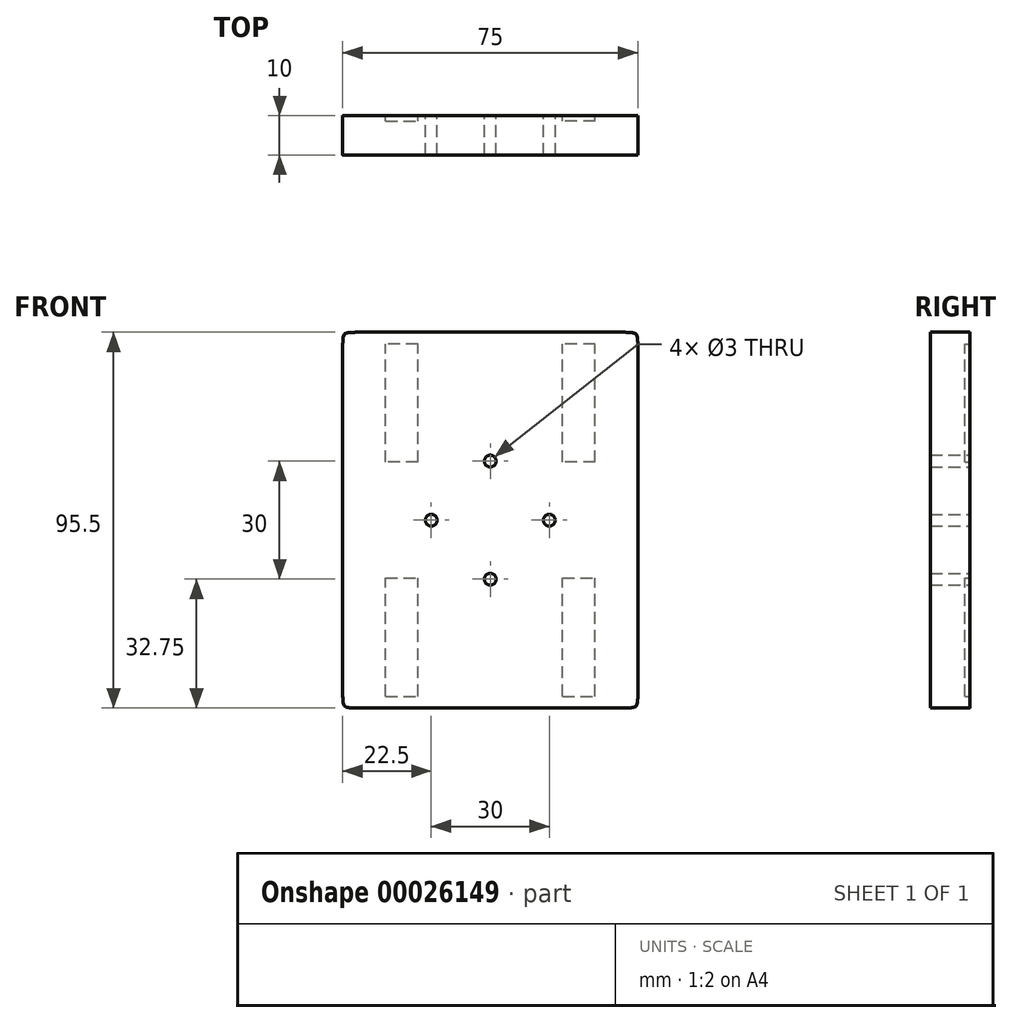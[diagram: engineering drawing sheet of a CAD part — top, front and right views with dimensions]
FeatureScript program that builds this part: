
annotation { "Feature Type Name" : "Feature", "Feature Type Description" : "" }
export const myFeature = defineFeature(function(context is Context, id is Id, definition is map)
    precondition{}
    {
        {
            var Q0;
            Q0=qCreatedBy(makeId("Front.planeOp"),FACE);
            var sketch = newSketch(context, id + "F0", { "sketchPlane" : qUnion([Q0])});
            skLineSegment(sketch, "E0.rect.bottom", {"start": v(37.5, -47.75) * mm, "end": v(-37.5, -47.75) * mm});
            skLineSegment(sketch, "E0.rect.top", {"start": v(37.5, 47.75) * mm, "end": v(-37.5, 47.75) * mm});
            skLineSegment(sketch, "E0.rect.left", {"start": v(37.5, -47.75) * mm, "end": v(37.5, 47.75) * mm});
            skLineSegment(sketch, "E0.rect.right", {"start": v(-37.5, -47.75) * mm, "end": v(-37.5, 47.75) * mm});
            skPoint(sketch, "E0.rect.middle", {"position": v(0, 0) * mm});
            skLineSegment(sketch, "E1", {"start": v(0, 15) * mm, "end": v(0, -15) * mm, "construction": true});
            skLineSegment(sketch, "E2", {"start": v(15, 0) * mm, "end": v(-15, 0) * mm, "construction": true});
            skCircle(sketch, "E3", {"center": v(0, 15) * mm, "radius": 1.5 * mm});
            skCircle(sketch, "E4", {"center": v(-15, 0) * mm, "radius": 1.5 * mm});
            skCircle(sketch, "E5", {"center": v(15, 0) * mm, "radius": 1.5 * mm});
            skCircle(sketch, "E6", {"center": v(0, -15) * mm, "radius": 1.5 * mm});
            skPoint(sketch, "E7.orphan", {"position": v(0, 47.75) * mm});
            skPoint(sketch, "E8.orphan", {"position": v(-37.5, 0) * mm});
            skPoint(sketch, "E9.orphan", {"position": v(0, -47.75) * mm});
            skPoint(sketch, "E10.orphan", {"position": v(37.5, 0) * mm});
            skLineSegment(sketch, "E11", {"start": v(22.5, 47.75) * mm, "end": v(22.5, -47.75) * mm, "construction": true});
            skLineSegment(sketch, "E12", {"start": v(-22.5, 47.75) * mm, "end": v(-22.5, -47.75) * mm, "construction": true});
            skLineSegment(sketch, "E13", {"start": v(-22.5, -47.75) * mm, "end": v(22.5, 47.75) * mm, "construction": true});
            skLineSegment(sketch, "E14.rect.bottom", {"start": v(-18.37, 14.75) * mm, "end": v(-26.62, 14.75) * mm});
            skLineSegment(sketch, "E14.rect.top", {"start": v(-18.38, 44.75) * mm, "end": v(-26.63, 44.75) * mm});
            skLineSegment(sketch, "E14.rect.left", {"start": v(-18.37, 14.75) * mm, "end": v(-18.38, 44.75) * mm});
            skLineSegment(sketch, "E14.rect.right", {"start": v(-26.62, 14.75) * mm, "end": v(-26.63, 44.75) * mm});
            skPoint(sketch, "E14.rect.middle", {"position": v(-22.5, 29.75) * mm});
            skLineSegment(sketch, "E15.rect.bottom", {"start": v(-26.62, -44.75) * mm, "end": v(-18.37, -44.75) * mm});
            skLineSegment(sketch, "E15.rect.top", {"start": v(-26.62, -14.75) * mm, "end": v(-18.38, -14.75) * mm});
            skLineSegment(sketch, "E15.rect.left", {"start": v(-26.62, -44.75) * mm, "end": v(-26.62, -14.75) * mm});
            skLineSegment(sketch, "E15.rect.right", {"start": v(-18.37, -44.75) * mm, "end": v(-18.38, -14.75) * mm});
            skPoint(sketch, "E15.rect.middle", {"position": v(-22.5, -29.75) * mm});
            skLineSegment(sketch, "E16.rect.bottom", {"start": v(26.62, 14.75) * mm, "end": v(18.37, 14.75) * mm});
            skLineSegment(sketch, "E16.rect.top", {"start": v(26.62, 44.75) * mm, "end": v(18.37, 44.75) * mm});
            skLineSegment(sketch, "E16.rect.left", {"start": v(26.62, 14.75) * mm, "end": v(26.62, 44.75) * mm});
            skLineSegment(sketch, "E16.rect.right", {"start": v(18.37, 14.75) * mm, "end": v(18.37, 44.75) * mm});
            skPoint(sketch, "E16.rect.middle", {"position": v(22.5, 29.75) * mm});
            skLineSegment(sketch, "E17.rect.bottom", {"start": v(18.38, -44.75) * mm, "end": v(26.63, -44.75) * mm});
            skLineSegment(sketch, "E17.rect.top", {"start": v(18.37, -14.75) * mm, "end": v(26.62, -14.75) * mm});
            skLineSegment(sketch, "E17.rect.left", {"start": v(18.38, -44.75) * mm, "end": v(18.37, -14.75) * mm});
            skLineSegment(sketch, "E17.rect.right", {"start": v(26.63, -44.75) * mm, "end": v(26.62, -14.75) * mm});
            skPoint(sketch, "E17.rect.middle", {"position": v(22.5, -29.75) * mm});
            skLineSegment(sketch, "E18", {"start": v(-37.5, 44.75) * mm, "end": v(37.5, 44.75) * mm, "construction": true});
            skLineSegment(sketch, "E19", {"start": v(37.5, -44.75) * mm, "end": v(-37.5, -44.75) * mm, "construction": true});
            skSolve(sketch);
        }
        {
            var Q0;
            Q0=makeQuery(id+"F0.imprint","IMPRINT",FACE,{"disambiguationData":[TD([[makeQuery(id+"F0.imprint","IMPRINT",EDGE,{"derivedFrom":sQuery(id+"F0.wireOp",EDGE,"E16.rect.bottom")}),-1.0]])]});
            var Q1;
            Q1=makeQuery(id+"F0.imprint","IMPRINT",FACE,{"disambiguationData":[TD([[makeQuery(id+"F0.imprint","IMPRINT",EDGE,{"derivedFrom":sQuery(id+"F0.wireOp",EDGE,"E14.rect.bottom")}),-1.0]])]});
            var Q2;
            Q2=makeQuery(id+"F0.imprint","IMPRINT",FACE,{"disambiguationData":[TD([[makeQuery(id+"F0.imprint","IMPRINT",EDGE,{"derivedFrom":sQuery(id+"F0.wireOp",EDGE,"E15.rect.bottom")}),1.0]])]});
            var Q3;
            Q3=makeQuery(id+"F0.imprint","IMPRINT",FACE,{"disambiguationData":[TD([[makeQuery(id+"F0.imprint","IMPRINT",EDGE,{"derivedFrom":sQuery(id+"F0.wireOp",EDGE,"E17.rect.bottom")}),1.0]])]});
            var Q4;
            Q4=makeQuery(id+"F0.imprint","IMPRINT",FACE,{"disambiguationData":[TD([[makeQuery(id+"F0.imprint","IMPRINT",EDGE,{"derivedFrom":sQuery(id+"F0.wireOp",EDGE,"E0.rect.bottom")}),-1.0]])]});
            extrude(context, id + "F1", {"entities" : qUnion([Q0, Q1, Q2, Q3, Q4]), "depth" : 10 * mm});
        }
        {
            var Q0;
            Q0=makeQuery(id+"F0.imprint","IMPRINT",FACE,{"disambiguationData":[TD([[makeQuery(id+"F0.imprint","IMPRINT",EDGE,{"derivedFrom":sQuery(id+"F0.wireOp",EDGE,"E16.rect.bottom")}),-1.0]])]});
            var Q1;
            Q1=makeQuery(id+"F0.imprint","IMPRINT",FACE,{"disambiguationData":[TD([[makeQuery(id+"F0.imprint","IMPRINT",EDGE,{"derivedFrom":sQuery(id+"F0.wireOp",EDGE,"E17.rect.bottom")}),1.0]])]});
            var Q2;
            Q2=makeQuery(id+"F0.imprint","IMPRINT",FACE,{"disambiguationData":[TD([[makeQuery(id+"F0.imprint","IMPRINT",EDGE,{"derivedFrom":sQuery(id+"F0.wireOp",EDGE,"E14.rect.bottom")}),-1.0]])]});
            var Q3;
            Q3=makeQuery(id+"F0.imprint","IMPRINT",FACE,{"disambiguationData":[TD([[makeQuery(id+"F0.imprint","IMPRINT",EDGE,{"derivedFrom":sQuery(id+"F0.wireOp",EDGE,"E15.rect.bottom")}),1.0]])]});
            extrude(context, id + "F2", {"entities" : qUnion([Q0, Q1, Q2, Q3]), "operationType" : NewBodyOperationType.REMOVE, "depth" : 1.3 * mm});
        }
        {
            var Q0;
            Q0=makeQuery(id+"F1.opExtrude","SWEPT_EDGE",EDGE,{"disambiguationData":[OSD([sQuery(id+"F0.wireOp",EDGE,"E0.rect.top"),sQuery(id+"F0.wireOp",EDGE,"E0.rect.left")])]});
            var Q1;
            Q1=makeQuery(id+"F1.opExtrude","SWEPT_EDGE",EDGE,{"disambiguationData":[OSD([sQuery(id+"F0.wireOp",EDGE,"E0.rect.top"),sQuery(id+"F0.wireOp",EDGE,"E0.rect.right")])]});
            var Q2;
            Q2=makeQuery(id+"F1.opExtrude","SWEPT_EDGE",EDGE,{"disambiguationData":[OSD([sQuery(id+"F0.wireOp",EDGE,"E0.rect.bottom"),sQuery(id+"F0.wireOp",EDGE,"E0.rect.right")])]});
            var Q3;
            Q3=makeQuery(id+"F1.opExtrude","SWEPT_EDGE",EDGE,{"disambiguationData":[OSD([sQuery(id+"F0.wireOp",EDGE,"E0.rect.bottom"),sQuery(id+"F0.wireOp",EDGE,"E0.rect.left")])]});
            fillet(context, id + "F3", {"entities" : qUnion([Q0, Q1, Q2, Q3]), "radius" : 5 * mm, "tangentPropagation" : true, "rho" : 0.8, "crossSection" : FilletCrossSection.CONIC, "allowEdgeOverflow" : false});
        }
    });
